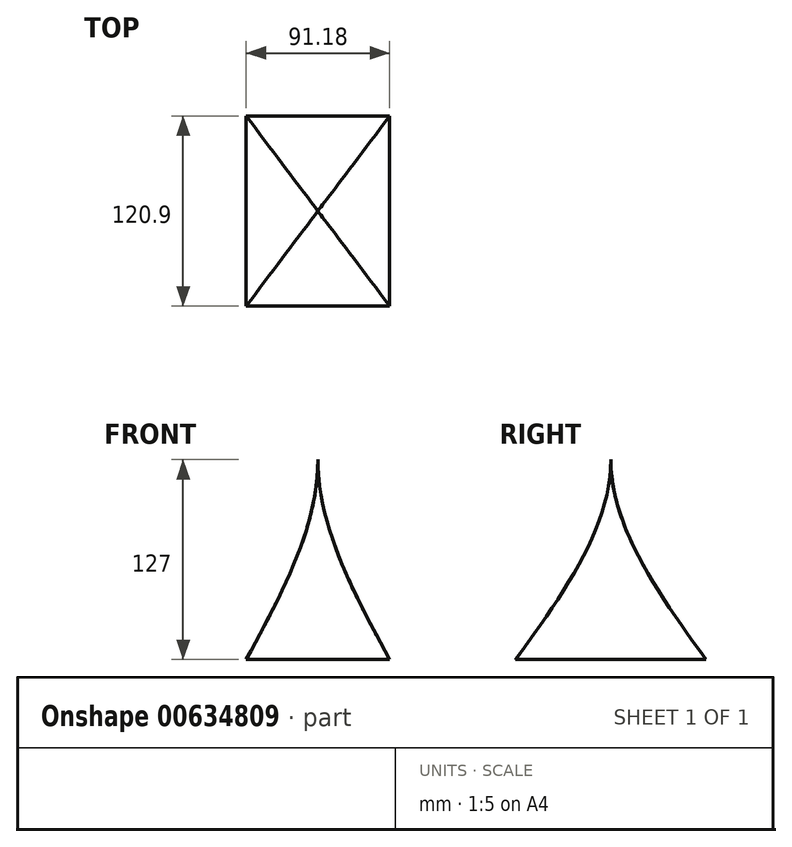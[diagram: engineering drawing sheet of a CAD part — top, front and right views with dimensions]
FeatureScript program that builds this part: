
annotation { "Feature Type Name" : "Feature", "Feature Type Description" : "" }
export const myFeature = defineFeature(function(context is Context, id is Id, definition is map)
    precondition{}
    {
        {
            var Q0;
            Q0=qCreatedBy(makeId("Top.planeOp"),FACE);
            var sketch = newSketch(context, id + "F0", { "sketchPlane" : qUnion([Q0])});
            skLineSegment(sketch, "E0.bottom", {"start": v(45.59, 60.45) * mm, "end": v(-45.59, 60.45) * mm});
            skLineSegment(sketch, "E0.top", {"start": v(45.59, -60.45) * mm, "end": v(-45.59, -60.45) * mm});
            skLineSegment(sketch, "E0.left", {"start": v(45.59, 60.45) * mm, "end": v(45.59, -60.45) * mm});
            skLineSegment(sketch, "E0.right", {"start": v(-45.59, 60.45) * mm, "end": v(-45.59, -60.45) * mm});
            skPoint(sketch, "E0.middle", {"position": v(0, 0) * mm});
            skSolve(sketch);
        }
        {
            var Q0;
            Q0=qCreatedBy(makeId("Top.planeOp"),FACE);
            cPlane(context, id + "F1", {"entities" : qUnion([Q0]), "cplaneType" : CPlaneType.OFFSET, "offset" : 127 * mm, "width" : 152.4 * mm, "height" : 152.4 * mm});
        }
        {
            var Q0;
            Q0=qCreatedBy(id+"F1.planeOp",FACE);
            var sketch = newSketch(context, id + "F2", { "sketchPlane" : qUnion([Q0])});
            skPoint(sketch, "E1.middle", {"position": v(0, 0) * mm});
            skCircle(sketch, "E2", {"center": v(0, 0) * mm, "radius": 31.3 * mm});
            skSolve(sketch);
        }
        {
            var Q0;
            Q0=sQuery(id+"F2.wireOp",VERTEX,"E1.middle");
            var Q1;
            Q1=makeQuery(id+"F0.imprint","IMPRINT",FACE,{"disambiguationData":[TD([[makeQuery(id+"F0.imprint","IMPRINT",EDGE,{"derivedFrom":sQuery(id+"F0.wireOp",EDGE,"E0.bottom")}),1.0]])]});
            loft(context, id + "F3", {"startCondition" : LoftEndDerivativeType.NORMAL_TO_PROFILE, "startMagnitude" : 1, "sheetProfilesArray" : [{ "sheetProfileEntities" : qUnion([Q0]) }, { "sheetProfileEntities" : qUnion([Q1]) }]});
        }
    });
